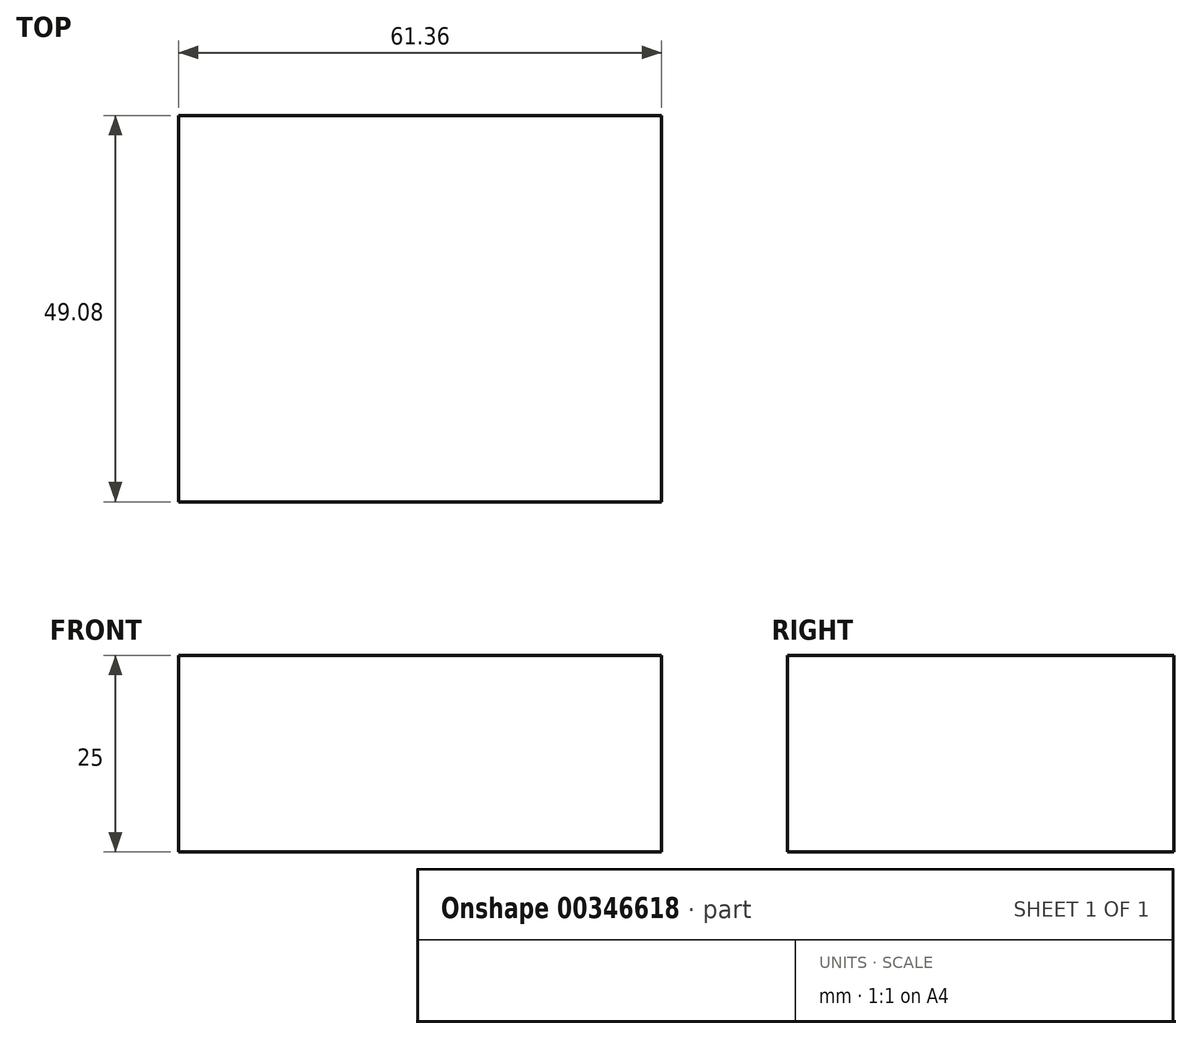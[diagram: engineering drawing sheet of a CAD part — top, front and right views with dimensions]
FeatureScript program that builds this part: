
annotation { "Feature Type Name" : "Feature", "Feature Type Description" : "" }
export const myFeature = defineFeature(function(context is Context, id is Id, definition is map)
    precondition{}
    {
        {
            var Q0;
            Q0=qCreatedBy(makeId("Top.planeOp"),FACE);
            var sketch = newSketch(context, id + "F0", { "sketchPlane" : qUnion([Q0])});
            skLineSegment(sketch, "E0.bottom", {"start": v(-31.3, 23.45) * mm, "end": v(30.07, 23.45) * mm});
            skLineSegment(sketch, "E0.top", {"start": v(-31.3, -25.63) * mm, "end": v(30.07, -25.63) * mm});
            skLineSegment(sketch, "E0.left", {"start": v(-31.3, 23.45) * mm, "end": v(-31.3, -25.63) * mm});
            skLineSegment(sketch, "E0.right", {"start": v(30.07, 23.45) * mm, "end": v(30.07, -25.63) * mm});
            skLineSegment(sketch, "E1.bottom", {"start": v(30.07, 23.45) * mm, "end": v(30.07, 23.45) * mm});
            skLineSegment(sketch, "E1.top", {"start": v(30.07, -25.63) * mm, "end": v(30.07, -25.63) * mm});
            skSolve(sketch);
        }
        {
            var Q0;
            Q0=makeQuery(id+"F0.imprint","IMPRINT",FACE,{"disambiguationData":[TD([[makeQuery(id+"F0.imprint","IMPRINT",EDGE,{"derivedFrom":sQuery(id+"F0.wireOp",EDGE,"E0.bottom")}),-1.0]])]});
            var sketch = newSketch(context, id + "F1", { "sketchPlane" : qUnion([Q0])});
            skSolve(sketch);
        }
        {
            var Q0;
            Q0 = qSketchRegion(id + "F1", true);
            var Q1;
            Q1=makeQuery(id+"F1.imprint","IMPRINT",FACE,{"disambiguationData":[TD([[makeQuery(id+"F1.imprint","IMPRINT",EDGE,{"derivedFrom":makeQuery(id+"F0.imprint","IMPRINT",EDGE,{"derivedFrom":sQuery(id+"F0.wireOp",EDGE,"E0.bottom")})}),-1.0]])]});
            extrude(context, id + "F2", {"entities" : qUnion([Q0, Q1]), "depth" : 25 * mm});
        }
    });
